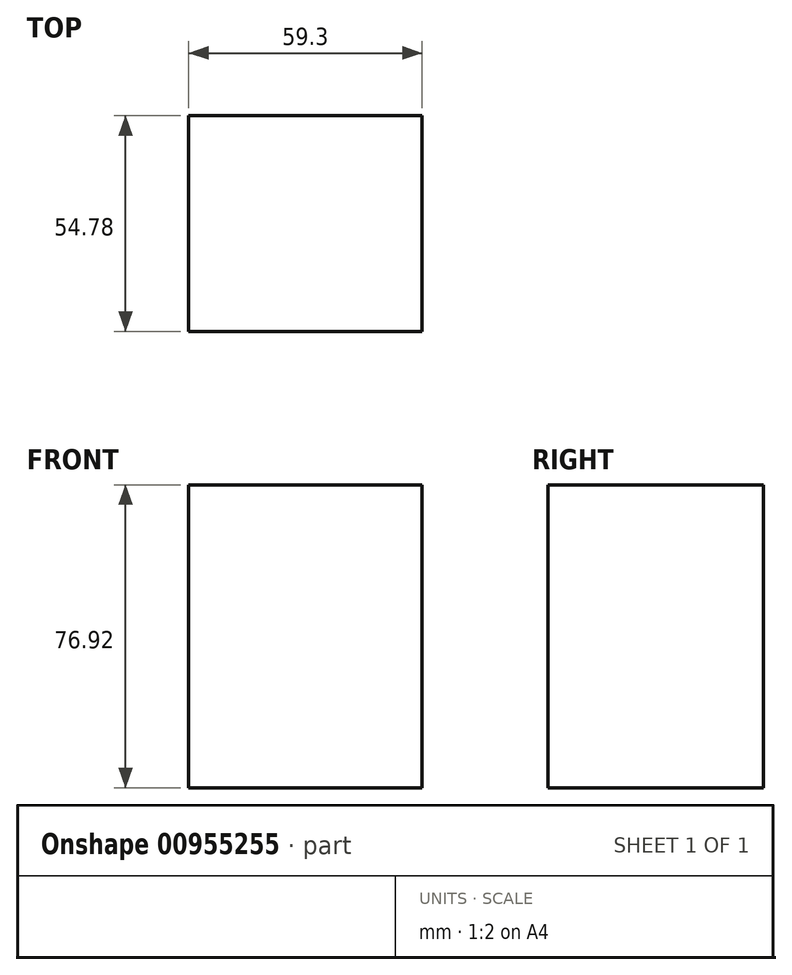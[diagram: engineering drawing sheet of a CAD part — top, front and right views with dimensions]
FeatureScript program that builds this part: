
annotation { "Feature Type Name" : "Feature", "Feature Type Description" : "" }
export const myFeature = defineFeature(function(context is Context, id is Id, definition is map)
    precondition{}
    {
        {
            var Q0;
            Q0=qCreatedBy(makeId("Top.planeOp"),FACE);
            var sketch = newSketch(context, id + "F0", { "sketchPlane" : qUnion([Q0])});
            skLineSegment(sketch, "E0.bottom", {"start": v(-59.3, -54.78) * mm, "end": v(0, -54.78) * mm});
            skLineSegment(sketch, "E0.top", {"start": v(-59.3, 0) * mm, "end": v(0, 0) * mm});
            skLineSegment(sketch, "E0.left", {"start": v(-59.3, -54.78) * mm, "end": v(-59.3, 0) * mm});
            skLineSegment(sketch, "E0.right", {"start": v(0, -54.78) * mm, "end": v(0, 0) * mm});
            skSolve(sketch);
        }
        {
            var Q0;
            Q0=makeQuery(id+"F0.imprint","IMPRINT",FACE,{"disambiguationData":[TD([[makeQuery(id+"F0.imprint","IMPRINT",EDGE,{"derivedFrom":sQuery(id+"F0.wireOp",EDGE,"E0.bottom")}),1.0]])]});
            extrude(context, id + "F1", {"entities" : qUnion([Q0]), "oppositeDirection" : true, "depth" : 76.92 * mm, "offsetDistance" : 25.4 * mm});
        }
    });
